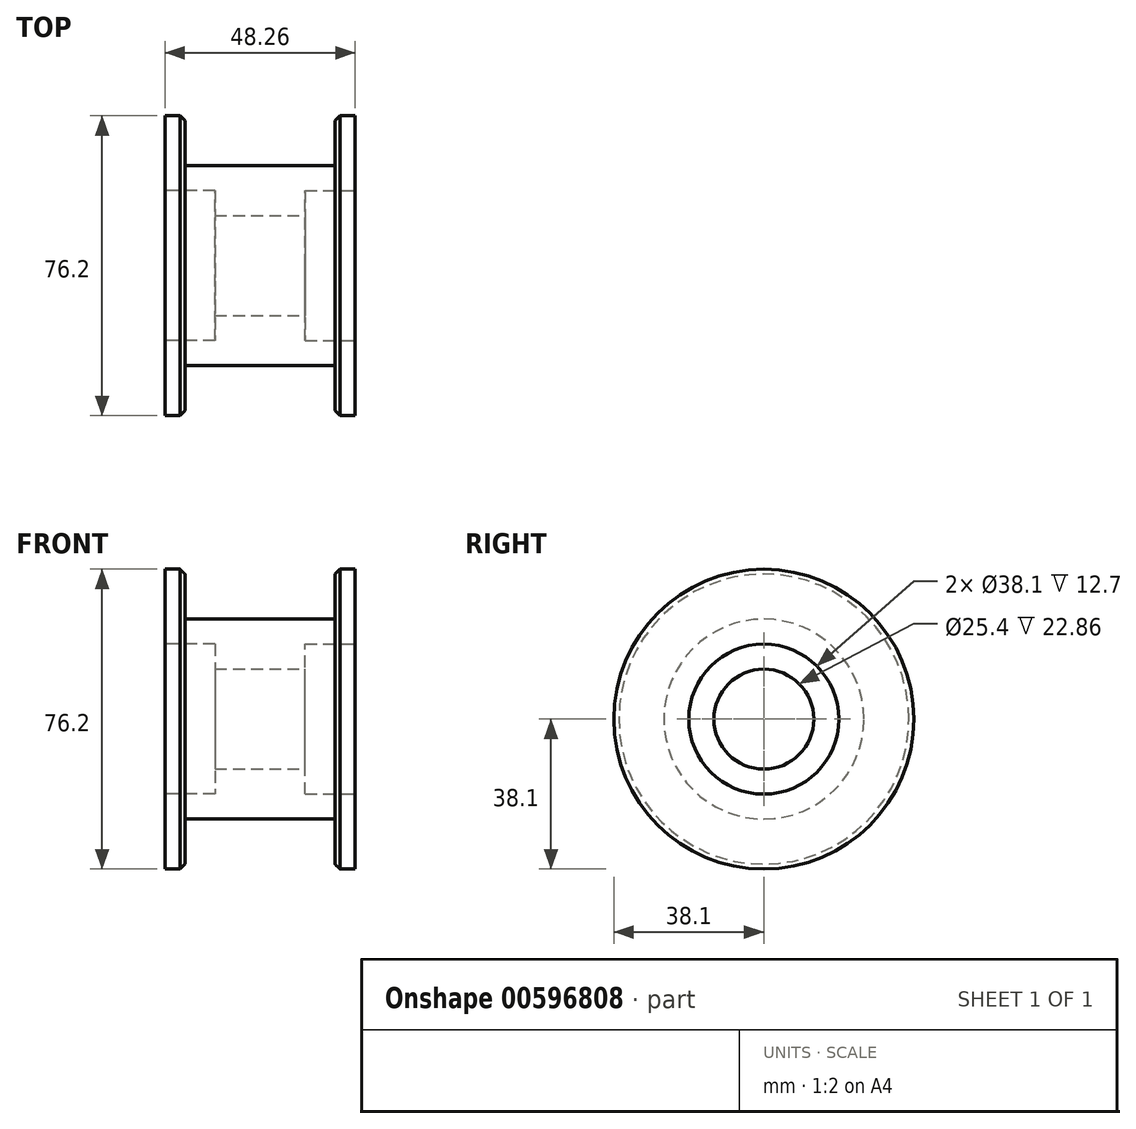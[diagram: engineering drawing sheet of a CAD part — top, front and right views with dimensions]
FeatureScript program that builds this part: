
annotation { "Feature Type Name" : "Feature", "Feature Type Description" : "" }
export const myFeature = defineFeature(function(context is Context, id is Id, definition is map)
    precondition{}
    {
        {
            var Q0;
            Q0=qCreatedBy(makeId("Right.planeOp"),FACE);
            var sketch = newSketch(context, id + "F0", { "sketchPlane" : qUnion([Q0])});
            skCircle(sketch, "E0", {"center": v(0, 0) * mm, "radius": 25.4 * mm});
            skSolve(sketch);
        }
        {
            var Q0;
            Q0=makeQuery(id+"F0.imprint","IMPRINT",FACE,{"disambiguationData":[TD([[makeQuery(id+"F0.imprint","IMPRINT",EDGE,{"derivedFrom":sQuery(id+"F0.wireOp",EDGE,"E0")}),1.0]])]});
            extrude(context, id + "F1", {"entities" : qUnion([Q0]), "depth" : 38.1 * mm, "offsetDistance" : 25.4 * mm});
        }
        {
            var Q0;
            Q0=makeQuery(id+"F1.opExtrude","CAP_FACE",FACE,{"disambiguationData":[OSD([sQuery(id+"F0.wireOp",EDGE,"E0")])],"isStart":false});
            var sketch = newSketch(context, id + "F2", { "sketchPlane" : qUnion([Q0])});
            skCircle(sketch, "E1", {"center": v(0, 0) * mm, "radius": 38.1 * mm});
            skSolve(sketch);
        }
        {
            var Q0;
            Q0=makeQuery(id+"F2.imprint","IMPRINT",FACE,{"disambiguationData":[TD([[makeQuery(id+"F2.imprint","IMPRINT",EDGE,{"derivedFrom":sQuery(id+"F2.wireOp",EDGE,"E1")}),1.0]])]});
            var Q1;
            Q1=makeQuery(id+"F2.imprint","IMPRINT",FACE,{"disambiguationData":[TD([[makeQuery(id+"F2.imprint","IMPRINT",EDGE,{"derivedFrom":makeQuery(id+"F1.opExtrude","CAP_EDGE",EDGE,{"disambiguationData":[OSD([sQuery(id+"F0.wireOp",EDGE,"E0")])],"isStart":false})}),1.0]])]});
            extrude(context, id + "F3", {"entities" : qUnion([Q0, Q1]), "operationType" : NewBodyOperationType.ADD, "depth" : 5.08 * mm, "offsetDistance" : 25.4 * mm});
        }
        {
            var Q0;
            Q0=makeQuery(id+"F1.opExtrude","CAP_FACE",FACE,{"disambiguationData":[OSD([sQuery(id+"F0.wireOp",EDGE,"E0")])],"isStart":true});
            var sketch = newSketch(context, id + "F4", { "sketchPlane" : qUnion([Q0])});
            skCircle(sketch, "E2", {"center": v(0, 0) * mm, "radius": 38.1 * mm});
            skSolve(sketch);
        }
        {
            var Q0;
            Q0 = qSketchRegion(id + "F4", true);
            extrude(context, id + "F5", {"entities" : qUnion([Q0]), "operationType" : NewBodyOperationType.ADD, "depth" : 5.08 * mm, "offsetDistance" : 25.4 * mm});
        }
        {
            var Q0;
            Q0=makeQuery(id+"F5.opExtrude","CAP_FACE",FACE,{"disambiguationData":[OSD([sQuery(id+"F4.wireOp",EDGE,"E2")])],"isStart":false});
            var sketch = newSketch(context, id + "F6", { "sketchPlane" : qUnion([Q0])});
            skCircle(sketch, "E3", {"center": v(0, 0) * mm, "radius": 19.05 * mm});
            skSolve(sketch);
        }
        {
            var Q0;
            Q0=makeQuery(id+"F6.imprint","IMPRINT",FACE,{"disambiguationData":[TD([[makeQuery(id+"F6.imprint","IMPRINT",EDGE,{"derivedFrom":sQuery(id+"F6.wireOp",EDGE,"E3")}),1.0]])]});
            var Q1;
            Q1=makeQuery(id+"F3.opExtrude","CAP_FACE",FACE,{"disambiguationData":[OSD([sQuery(id+"F2.wireOp",EDGE,"E1")])],"isStart":false});
            extrude(context, id + "F7", {"entities" : qUnion([Q0, Q1]), "operationType" : NewBodyOperationType.REMOVE, "oppositeDirection" : true, "depth" : 12.7 * mm, "offsetDistance" : 25.4 * mm});
        }
        {
            var Q0;
            Q0=makeQuery(id+"F3.opExtrude","CAP_FACE",FACE,{"disambiguationData":[OSD([sQuery(id+"F2.wireOp",EDGE,"E1")])],"isStart":false});
            var sketch = newSketch(context, id + "F8", { "sketchPlane" : qUnion([Q0])});
            skCircle(sketch, "E4", {"center": v(0, 0) * mm, "radius": 19.05 * mm});
            skSolve(sketch);
        }
        {
            var Q0;
            Q0=makeQuery(id+"F8.imprint","IMPRINT",FACE,{"disambiguationData":[TD([[makeQuery(id+"F8.imprint","IMPRINT",EDGE,{"derivedFrom":sQuery(id+"F8.wireOp",EDGE,"E4")}),1.0]])]});
            extrude(context, id + "F9", {"entities" : qUnion([Q0]), "operationType" : NewBodyOperationType.REMOVE, "oppositeDirection" : true, "depth" : 12.7 * mm, "offsetDistance" : 25.4 * mm});
        }
        {
            var Q0;
            Q0=makeQuery(id+"F9.boolean.opBoolean","COPY",FACE,{"derivedFrom":makeQuery(id+"F9.opExtrude","CAP_FACE",FACE,{"disambiguationData":[OSD([sQuery(id+"F8.wireOp",EDGE,"E4")])],"isStart":false})});
            var sketch = newSketch(context, id + "F10", { "sketchPlane" : qUnion([Q0])});
            skCircle(sketch, "E5", {"center": v(0, 0) * mm, "radius": 12.7 * mm});
            skSolve(sketch);
        }
        {
            var Q0;
            Q0 = qSketchRegion(id + "F10", true);
            extrude(context, id + "F11", {"entities" : qUnion([Q0]), "operationType" : NewBodyOperationType.REMOVE, "endBound" : BoundingType.THROUGH_ALL, "oppositeDirection" : true, "depth" : 25.4 * mm, "offsetDistance" : 25.4 * mm});
        }
        {
            var Q0;
            Q0=makeQuery(id+"F5.opExtrude","CAP_EDGE",EDGE,{"disambiguationData":[OSD([sQuery(id+"F4.wireOp",EDGE,"E2")])],"isStart":true});
            var Q1;
            Q1=makeQuery(id+"F3.opExtrude","CAP_EDGE",EDGE,{"disambiguationData":[OSD([sQuery(id+"F2.wireOp",EDGE,"E1")])],"isStart":true});
            chamfer(context, id + "F12", {"entities" : qUnion([Q0, Q1]), "width" : 1.27 * mm, "tangentPropagation" : true});
        }
    });
